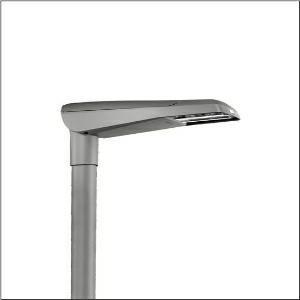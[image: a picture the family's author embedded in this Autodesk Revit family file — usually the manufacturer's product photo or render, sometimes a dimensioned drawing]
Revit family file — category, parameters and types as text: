
# Revit family: streetlight_sl_11_iq_micro___st1_0a_5xc1m51f08ce_5929
name_source: partatom
category: Lighting Fixtures
units: mm (PartAtom-declared; Revit-internal decimal feet)

## family parameters
Cut with Voids When Loaded = No
Host = Face
Light Source = No
Part Type = Normal
Room Calculation Point = No
Round Connector Dimension = Use Diameter
Shared = No

## types (1)
- --- (1 x LED, 1820 lm, 12.6 W, 3000K)
    Apparent Load = 13 VA
    CIE Flux Codes = 33 66 96 100 100
    Color Rendering = 70
    Color Temperature = 3000K
    Default Elevation = 1800 mm
    Description = Streetlight SL 11 iQ micro, mast luminaire, primary light control with 3 zone facetted reflector, of plastic, silver coated, highly specular, primary optical cover: cover, of PMMA, transparent, light distribution: ST1.0a, light emission: direct distribution, primary light characteristic: asymmetric, installation type: post-top, side-entry, lamps: LED, High Power LED, rated values: 1.820lm | 12,6W | 144,4lm/W (begin service life); end service life: 1.820lm | 12,9W; at 50% lumin. flux: 910lm | 6,8W | 133,8lm/W, colour temperature: 3000K, colour rendering: CRI > 70, light colour: 730, light setting 1 begin service life: 100% | 1.820lm | 12,6W | 144,4lm/W | 3.000K, light setting 1 end service life: 12,9W, further light settings possible, control: optimised constant luminous flux control (CLO 2.0), Desk-Remote (wireless, voltage-free reading and setting of iQ features in the workshop via application-optimized NFC function/RFID function), Light-Fading, Smart-Wire, Night-Set, Lumen-Switch, Temp-Guard, Auto-Match, Street-Remote, with cable H07RN-F 3x 1.5mm², mains connection: 230..240V, AC, 50/60Hz, connection cable pre-assembled, cable length: 5,5m, luminaire housing, of diecast aluminium, powder-coated, SITECO metallic grey (DB 702S), please order mast flange separately, inclination adjustable without tools: 0°, 5°, 10°, 15° (post-top) | 0°, -5°, -10°, -15° (side-entry), sealing non-destructively replaceable, multi-level sealing system, length: 600mm, width: 174mm, height: 116mm, mast flange for spigot size: 42mm (side-entry): 5XC10008XM4, 60/48mm (side-entry/post-top): 5XC10108XM2, 76/60mm (side-entry/post-top): 5XC10108XM1, equipment: standard, protection rating (complete): IP66, insulation class (complete): insulation class II (safety insulation), certification: CE, ENEC, ENEC+, VDE, impact resistance: IK10, permissible operating ambient temperature for outdoor applications: -25..+50°C, standard-compliant lighting for roads and squares, Environmental Product Declaration (EPD) tested and certified by an independent institute, packaging unit: 1 piece

Light Distribution: ST1.0a
    Height = 116 mm
    Lamp = 1 x LED
    Lamp Light Flux = 1820 lm
    Lamp Power = 12.6 W
    Lamp count = 1
    Length = 600 mm
    Luminous efficacy = 144 lm/W
    Manufacturer = Siteco
    ModVariant = No
    Model = 5XC1M51F08CE
    Number of Poles = 1
    OnlyDefault = Yes
    Power Factor = 1
    Product Name = Streetlight SL 11 iQ micro | ST1.0a
    Product group = mast luminaire | pylon top
    ProductGroupID = 6100
    Protection Class = Protection class II
    Protection Degree = IP 66
    RLX_Detail_Level = 1
    RLX_Emergency_Light_Flux = 0 lm
    RLX_Emergency_Type = 0
    RLX_Emergency_Type_DB = No
    RlxData = <blob elided: 26273 chars, md5=50e68a7c>
    Socket = socket
    Standby Power = 0 W
    System Light Flux = 1820 lm
    System Power = 13 W
    Type Comments = factory setting: luminous flux: 100 % | dim-lin: 254 | 229 mA
    Type Image = l_1006566.jpg
    URL = http://relux.com
    VarID = @adj_021559
    Voltage = 0 V
    Weight = 0.00 kg
    Width = 174 mm

## geometry (parser evidence)
native form markers: Blend x4, Sweep x11
no freeform markers — native parametric forms only
